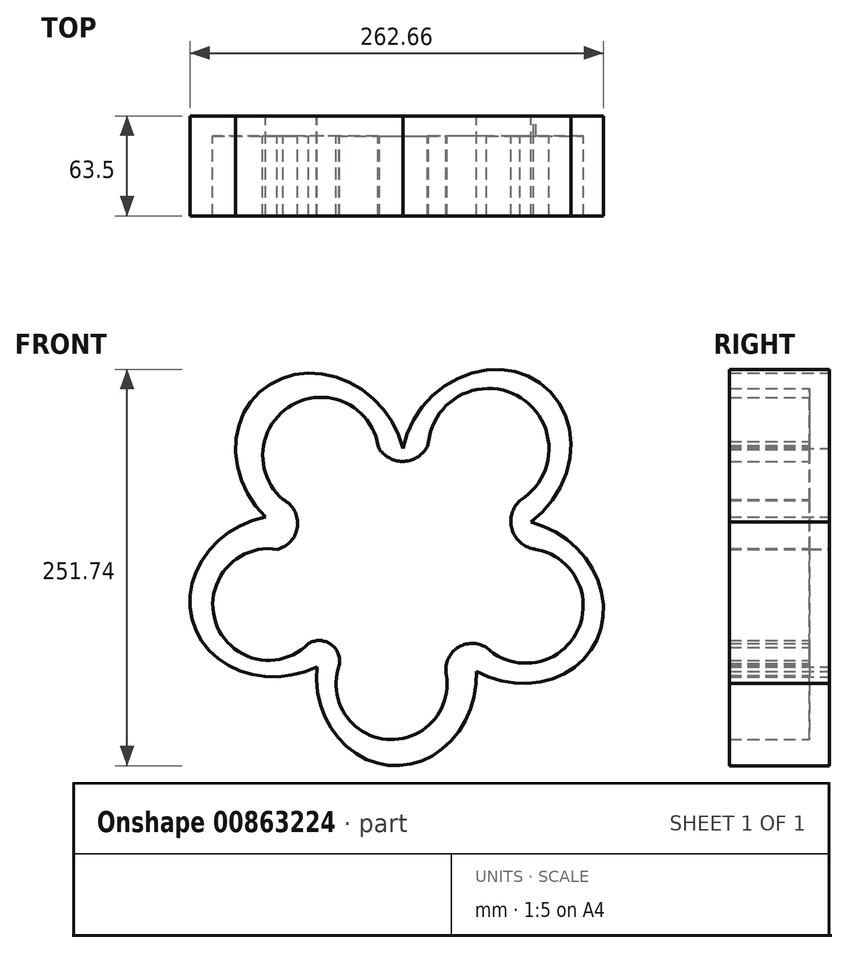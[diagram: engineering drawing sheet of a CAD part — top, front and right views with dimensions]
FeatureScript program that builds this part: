
annotation { "Feature Type Name" : "Feature", "Feature Type Description" : "" }
export const myFeature = defineFeature(function(context is Context, id is Id, definition is map)
    precondition{}
    {
        {
            var Q0;
            Q0=qCreatedBy(makeId("Front.planeOp"),FACE);
            var sketch = newSketch(context, id + "F0", { "sketchPlane" : qUnion([Q0])});
            skEllipticalArc(sketch, "E0", {});
            skEllipticalArc(sketch, "E1", {});
            skEllipticalArc(sketch, "E2", {});
            skEllipticalArc(sketch, "E3.trimOffspring", {});
            skEllipticalArc(sketch, "E4.trimOffspring", {});
            skArc(sketch, "E5", {"start": v(-79.45, 0) * mm, "mid": v(-118.58, -46.22) * mm, "end": v(-59.58, -59.86) * mm});
            skArc(sketch, "E6", {"start": v(-40.07, -73.64) * mm, "mid": v(-10.19, -120.7) * mm, "end": v(27.97, -80.05) * mm});
            skArc(sketch, "E7", {"start": v(53.5, -62.4) * mm, "mid": v(111.37, -51.55) * mm, "end": v(83.33, 0.23) * mm});
            skArc(sketch, "E8", {"start": v(74.8, 31.1) * mm, "mid": v(75.5, 96.08) * mm, "end": v(16.64, 68.53) * mm});
            skArc(sketch, "E9", {"start": v(-15.34, 65.9) * mm, "mid": v(-70, 91.75) * mm, "end": v(-75.62, 31.54) * mm});
            skPoint(sketch, "E9.startSnap0", {"position": v(-14.88, 92.19) * mm});
            skArc(sketch, "E10", {"start": v(-79.45, 0) * mm, "mid": v(-66.61, 14.44) * mm, "end": v(-75.62, 31.54) * mm});
            skArc(sketch, "E11", {"start": v(-40.07, -73.64) * mm, "mid": v(-45.3, -60.33) * mm, "end": v(-59.58, -59.86) * mm});
            skArc(sketch, "E12", {"start": v(53.5, -62.4) * mm, "mid": v(34.87, -62.75) * mm, "end": v(27.97, -80.05) * mm});
            skPoint(sketch, "E13.end.orphan", {"position": v(16.45, -36.7) * mm});
            skPoint(sketch, "E14.trimOffspring.start.orphan", {"position": v(-40.07, 3.36) * mm});
            skArc(sketch, "E15", {"start": v(74.8, 31.1) * mm, "mid": v(69.77, 12.31) * mm, "end": v(84.81, 0) * mm});
            skPoint(sketch, "E16.orphan", {"position": v(72.14, 0) * mm});
            skArc(sketch, "E17", {"start": v(-14.4, 63.5) * mm, "mid": v(1.33, 55.94) * mm, "end": v(15.94, 65.48) * mm});
            skPoint(sketch, "E18.orphan", {"position": v(-14.88, 57.47) * mm});
            skLineSegment(sketch, "E19", {"start": v(16.64, 68.53) * mm, "end": v(15.94, 65.48) * mm});
            skPoint(sketch, "E20.orphan", {"position": v(16.45, 66.55) * mm});
            skLineSegment(sketch, "E21", {"start": v(-15.34, 65.9) * mm, "end": v(-14.4, 63.5) * mm});
            const initialGuessF0  = {"E0": [0.053184581233435176, 0.05980964424407143, -0.6677543657542593, -0.7443816944391681, 0.057353400865375465, 0.0508, 1.3473643039255498, 5.305761862725996], "E1": [-0.0037369641061577577, -0.08005340971018807, 0.033050191191518925, 0.9994536932055452, 0.057353400865375465, 0.0508, 1.5041724461142187, 4.788160463571629], "E2": [-0.07810795254226847, -0.029522350821445182, 0.9504830914507381, 0.31077627461929574, 0.057353400865375465, 0.0508, 1.4453554044847408, 4.8639616894301305], "E3.trimOffspring": [0.07172549491273592, -0.0329841196631647, -0.8918450505831671, 0.4523410281527735, 0.057353400865375465, 0.0508, 1.537035080664463, 4.958079914265455], "E4.trimOffspring": [-0.05196478962945147, 0.05747124148066602, 0.6833504696365454, -0.7300904982586152, 0.057353400865375465, 0.0508, 1.000050522010815, 4.764757133445896]};
            skSetInitialGuess(sketch, initialGuessF0);
            skSolve(sketch);
        }
        {
            var Q0;
            Q0=makeQuery(id+"F0.imprint","IMPRINT",FACE,{"disambiguationData":[TD([[makeQuery(id+"F0.imprint","IMPRINT",EDGE,{"derivedFrom":sQuery(id+"F0.wireOp",EDGE,"E0")}),1.0]])]});
            extrude(context, id + "F1", {"entities" : qUnion([Q0]), "depth" : 63.5 * mm, "offsetDistance" : 25.4 * mm});
        }
        {
            var Q0;
            Q0=makeQuery(id+"F0.imprint","IMPRINT",FACE,{"disambiguationData":[TD([[makeQuery(id+"F0.imprint","IMPRINT",EDGE,{"derivedFrom":sQuery(id+"F0.wireOp",EDGE,"E5")}),1.0]])]});
            extrude(context, id + "F2", {"entities" : qUnion([Q0]), "operationType" : NewBodyOperationType.ADD, "depth" : 12.7 * mm, "offsetDistance" : 25.4 * mm});
        }
    });
